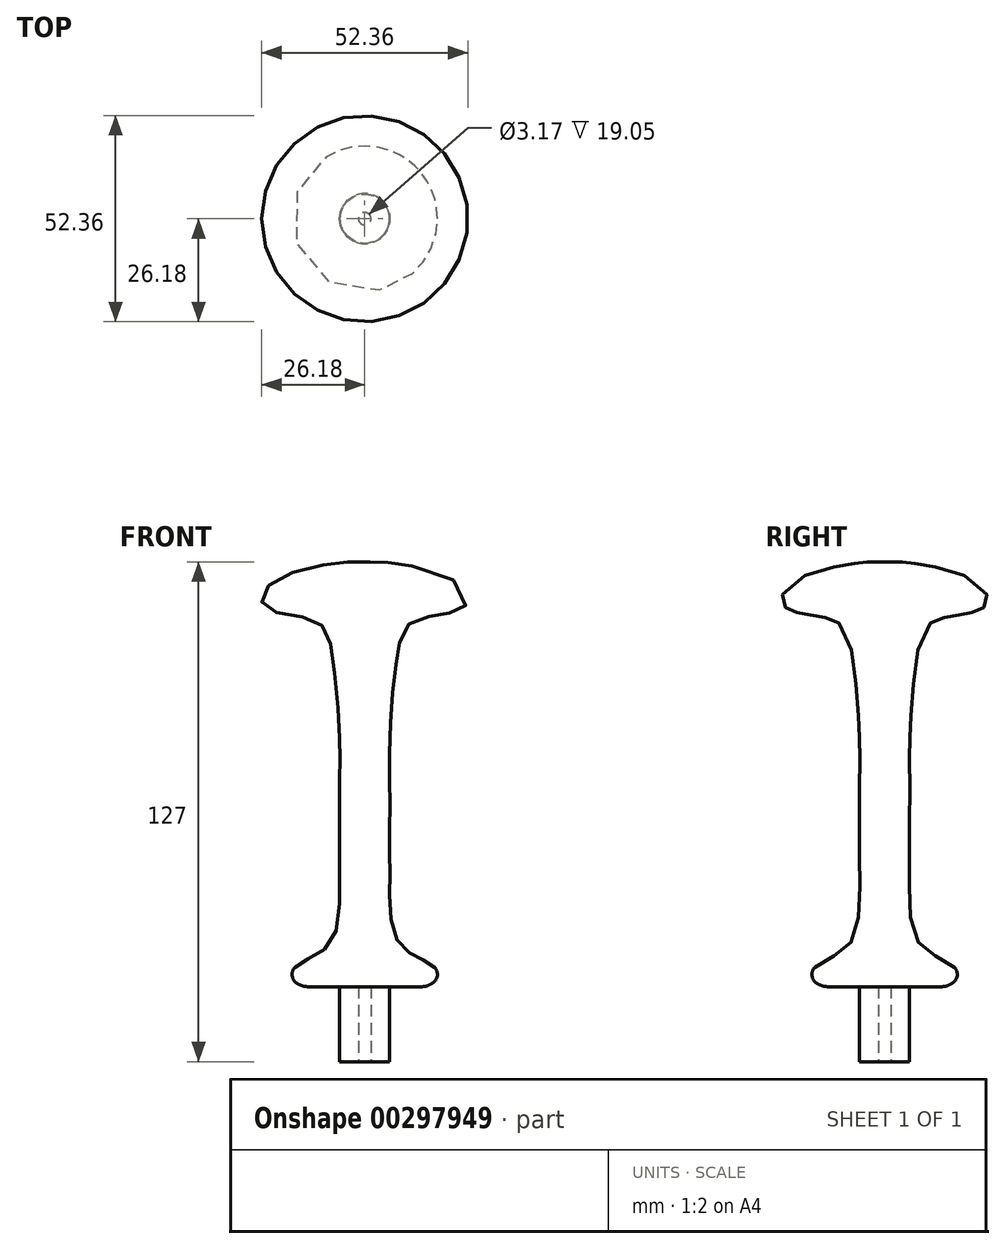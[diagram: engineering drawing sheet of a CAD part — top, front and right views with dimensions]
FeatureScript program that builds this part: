
annotation { "Feature Type Name" : "Feature", "Feature Type Description" : "" }
export const myFeature = defineFeature(function(context is Context, id is Id, definition is map)
    precondition{}
    {
        {
            var Q0;
            Q0=qCreatedBy(makeId("Front.planeOp"),FACE);
            var sketch = newSketch(context, id + "F0", { "sketchPlane" : qUnion([Q0])});
            skLineSegment(sketch, "E0", {"start": v(0, 0) * mm, "end": v(-6.35, 0) * mm});
            skLineSegment(sketch, "E1", {"start": v(-6.35, 0) * mm, "end": v(-6.35, 19.05) * mm});
            skLineSegment(sketch, "E2", {"start": v(-6.35, 19.05) * mm, "end": v(-19.05, 19.05) * mm});
            skLineSegment(sketch, "E3", {"start": v(-19.05, 19.05) * mm, "end": v(-19.05, 22.23) * mm});
            skLineSegment(sketch, "E4", {"start": v(0, 0) * mm, "end": v(0, 127) * mm, "construction": true});
            skLineSegment(sketch, "E5", {"start": v(7.26, 0) * mm, "end": v(7.26, 63.5) * mm, "construction": true});
            skLineSegment(sketch, "E6", {"start": v(-6.35, 19.05) * mm, "end": v(-6.35, 126.75) * mm, "construction": true});
            skPoint(sketch, "E7.2.internal.snap0", {"position": v(-12.7, 19.05) * mm});
            skFitSpline(sketch, "E8", {"points": [v(-19.05, 22.23) * mm, v(-14.91, 25.8) * mm, v(-8.24, 30.82) * mm, v(-6.35, 46.07) * mm, v(-6.35, 54.81) * mm, v(-6.35, 72.9) * mm, v(-6.35, 81.6) * mm, v(-8.46, 104.75) * mm, v(-12.93, 112.13) * mm, v(-25.4, 115.57) * mm, v(-24.02, 121.29) * mm, v(-6.35, 126.75) * mm, v(0, 127) * mm], "startDerivative": vector(58.39, 97.21) * mm, "endDerivative": vector(83.9, 0.38) * mm});
            skLineSegment(sketch, "E9", {"start": v(0, 0) * mm, "end": v(0, 127) * mm});
            skLineSegment(sketch, "E10", {"start": v(-25.4, 115.57) * mm, "end": v(0, 115.57) * mm, "construction": true});
            skSolve(sketch);
        }
        {
            var Q0;
            Q0=makeQuery(id+"F0.imprint","IMPRINT",FACE,{"disambiguationData":[TD([[makeQuery(id+"F0.imprint","IMPRINT",EDGE,{"derivedFrom":sQuery(id+"F0.wireOp",EDGE,"E0")}),-1.0]])]});
            var Q1;
            Q1=sQuery(id+"F0.wireOp",EDGE,"E9");
            revolve(context, id + "F1", {"entities" : qUnion([Q0]), "axis" : qUnion([Q1]), "revolveType" : RevolveType.FULL});
        }
        {
            var Q0;
            Q0=makeQuery(id+"F1.opRevolve","SWEPT_EDGE",EDGE,{"disambiguationData":[OSD([sQuery(id+"F0.wireOp",EDGE,"E2"),sQuery(id+"F0.wireOp",EDGE,"E3")])]});
            fillet(context, id + "F2", {"entities" : qUnion([Q0]), "radius" : 5.08 * mm, "tangentPropagation" : true, "allowEdgeOverflow" : false});
        }
        {
            var Q0;
            Q0=makeQuery(id+"F2.opFillet","BLEND_EDGE",EDGE,{"blendedFrom":[makeQuery(id+"F1.opRevolve","SWEPT_EDGE",EDGE,{"disambiguationData":[OSD([sQuery(id+"F0.wireOp",EDGE,"E2"),sQuery(id+"F0.wireOp",EDGE,"E3")])]}),makeQuery(id+"F1.opRevolve","SWEPT_FACE",FACE,{"disambiguationData":[OSD([sQuery(id+"F0.wireOp",EDGE,"E8")])]})],"blendedInto":[makeQuery(id+"F1.opRevolve","SWEPT_FACE",FACE,{"disambiguationData":[OSD([sQuery(id+"F0.wireOp",EDGE,"E8")])]})]});
            fillet(context, id + "F3", {"entities" : qUnion([Q0]), "radius" : 2.54 * mm, "tangentPropagation" : true, "allowEdgeOverflow" : false});
        }
        {
            var Q0;
            Q0=makeQuery(id+"F1.opRevolve","SWEPT_FACE",FACE,{"disambiguationData":[OSD([sQuery(id+"F0.wireOp",EDGE,"E0")])]});
            var sketch = newSketch(context, id + "F4", { "sketchPlane" : qUnion([Q0])});
            skCircle(sketch, "E11", {"center": v(0, 0) * mm, "radius": 1.59 * mm});
            skSolve(sketch);
        }
        {
            var Q0;
            Q0 = qSketchRegion(id + "F4", true);
            extrude(context, id + "F5", {"entities" : qUnion([Q0]), "operationType" : NewBodyOperationType.REMOVE, "oppositeDirection" : true, "depth" : 19.05 * mm});
        }
    });
